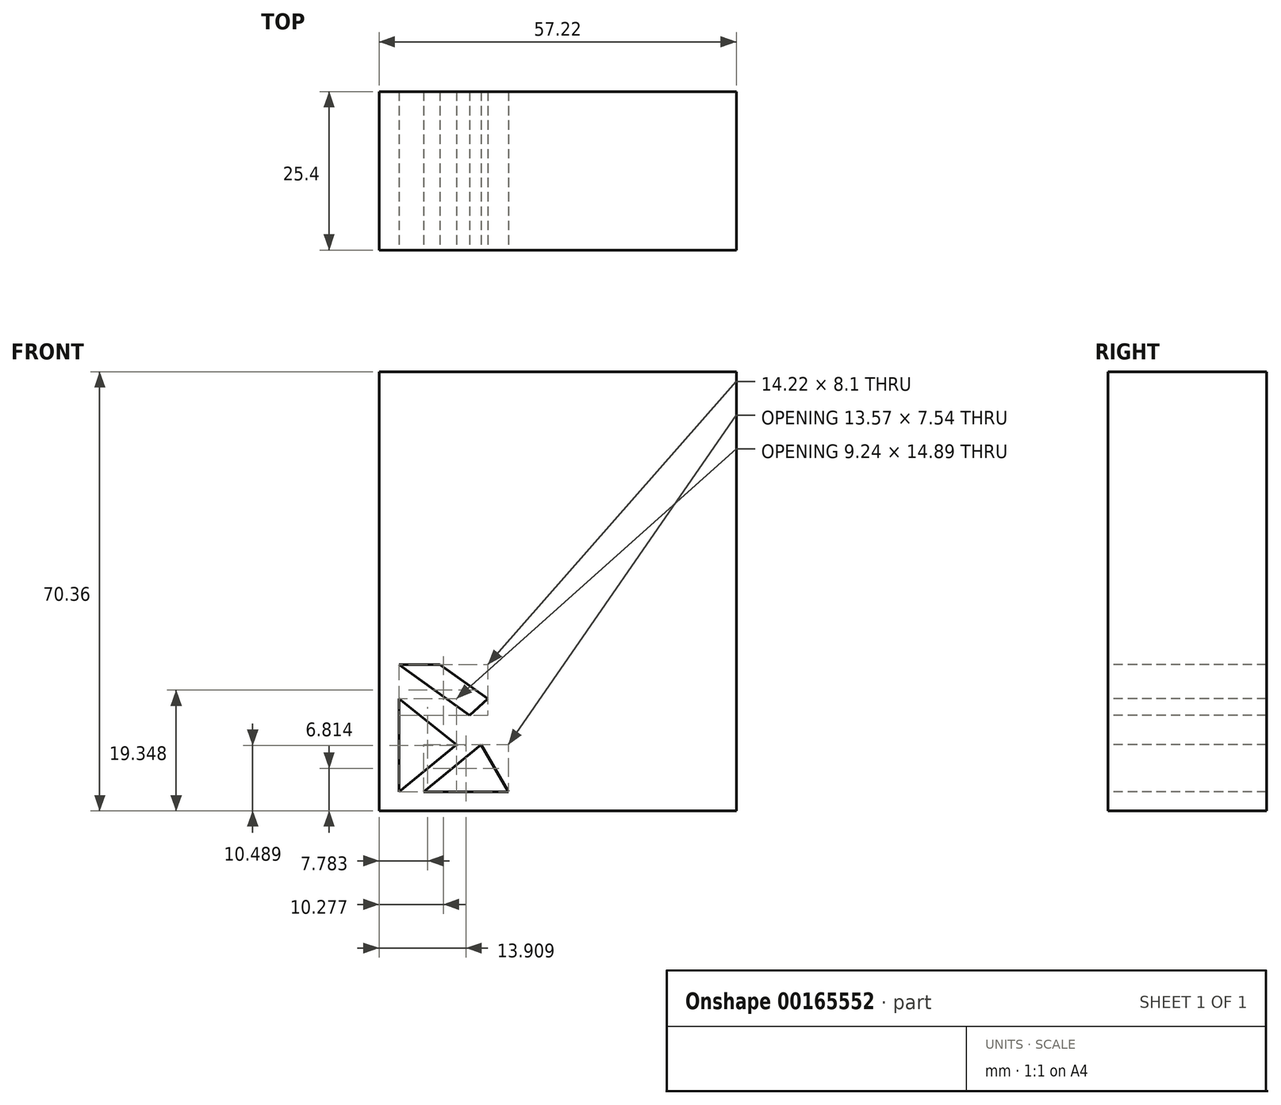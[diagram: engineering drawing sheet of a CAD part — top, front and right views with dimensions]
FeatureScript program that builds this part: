
annotation { "Feature Type Name" : "Feature", "Feature Type Description" : "" }
export const myFeature = defineFeature(function(context is Context, id is Id, definition is map)
    precondition{}
    {
        {
            var Q0;
            Q0=qCreatedBy(makeId("Front.planeOp"),FACE);
            var sketch = newSketch(context, id + "F0", { "sketchPlane" : qUnion([Q0])});
            skLineSegment(sketch, "E0.bottom", {"start": v(-28.61, -35.18) * mm, "end": v(28.61, -35.18) * mm});
            skLineSegment(sketch, "E0.top", {"start": v(-28.61, 35.18) * mm, "end": v(28.61, 35.18) * mm});
            skLineSegment(sketch, "E0.left", {"start": v(-28.61, -35.18) * mm, "end": v(-28.61, 35.18) * mm});
            skLineSegment(sketch, "E0.right", {"start": v(28.61, -35.18) * mm, "end": v(28.61, 35.18) * mm});
            skPoint(sketch, "E0.middle", {"position": v(0, 0) * mm});
            skSolve(sketch);
        }
        {
            var Q0;
            Q0 = qSketchRegion(id + "F0", true);
            extrude(context, id + "F1", {"entities" : qUnion([Q0]), "depth" : 25.4 * mm});
        }
        {
            var Q0;
            Q0=makeQuery(id+"F1.opExtrude","CAP_FACE",FACE,{"disambiguationData":[OSD([sQuery(id+"F0.wireOp",EDGE,"E0.bottom"),sQuery(id+"F0.wireOp",EDGE,"E0.top"),sQuery(id+"F0.wireOp",EDGE,"E0.left"),sQuery(id+"F0.wireOp",EDGE,"E0.right")])],"isStart":false});
            var sketch = newSketch(context, id + "F2", { "sketchPlane" : qUnion([Q0])});
            skLineSegment(sketch, "E1", {"start": v(-25.44, -32.14) * mm, "end": v(-25.44, -17.25) * mm});
            skLineSegment(sketch, "E2", {"start": v(-25.44, -17.25) * mm, "end": v(-16.2, -24.6) * mm});
            skLineSegment(sketch, "E3", {"start": v(-16.2, -24.6) * mm, "end": v(-25.44, -32.14) * mm});
            skLineSegment(sketch, "E4", {"start": v(-21.49, -32.14) * mm, "end": v(-12.25, -24.6) * mm});
            skLineSegment(sketch, "E5", {"start": v(-12.25, -24.6) * mm, "end": v(-7.92, -32.14) * mm});
            skLineSegment(sketch, "E6", {"start": v(-7.92, -32.14) * mm, "end": v(-21.49, -32.14) * mm});
            skLineSegment(sketch, "E7", {"start": v(-14.14, -19.88) * mm, "end": v(-25.44, -11.78) * mm});
            skLineSegment(sketch, "E8", {"start": v(-25.44, -11.78) * mm, "end": v(-18.85, -11.78) * mm});
            skLineSegment(sketch, "E9", {"start": v(-18.85, -11.78) * mm, "end": v(-11.22, -17.25) * mm});
            skLineSegment(sketch, "E10", {"start": v(-11.22, -17.25) * mm, "end": v(-14.14, -19.88) * mm});
            skSolve(sketch);
        }
        {
            var Q0;
            Q0=makeQuery(id+"F2.imprint","IMPRINT",FACE,{"disambiguationData":[TD([[makeQuery(id+"F2.imprint","IMPRINT",EDGE,{"derivedFrom":sQuery(id+"F2.wireOp",EDGE,"E7")}),-1.0]])]});
            var Q1;
            Q1=makeQuery(id+"F2.imprint","IMPRINT",FACE,{"disambiguationData":[TD([[makeQuery(id+"F2.imprint","IMPRINT",EDGE,{"derivedFrom":sQuery(id+"F2.wireOp",EDGE,"E1")}),-1.0]])]});
            var Q2;
            Q2=makeQuery(id+"F2.imprint","IMPRINT",FACE,{"disambiguationData":[TD([[makeQuery(id+"F2.imprint","IMPRINT",EDGE,{"derivedFrom":sQuery(id+"F2.wireOp",EDGE,"E4")}),-1.0]])]});
            extrude(context, id + "F3", {"entities" : qUnion([Q0, Q1, Q2]), "operationType" : NewBodyOperationType.REMOVE, "endBound" : BoundingType.THROUGH_ALL, "oppositeDirection" : true, "depth" : 25.4 * mm});
        }
    });
